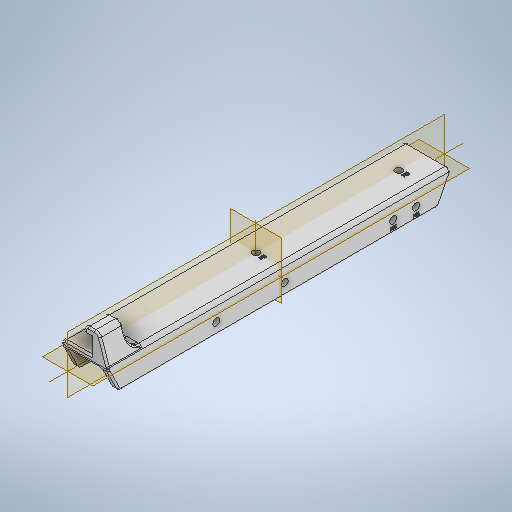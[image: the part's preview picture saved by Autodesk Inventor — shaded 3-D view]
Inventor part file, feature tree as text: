
AUTODESK INVENTOR PART (.ipt)
format: ipt  version: 2025 (Build 290162000, 162)  size: 669,696 bytes
history: native  units: mm
features: sketch x7, fillet x6, hole x3, pattern_linear x3, extrude x2, chamfer x2, emboss x2, projected_geometry x1
ambient origin geometry x8: Origin, YZ Plane, XZ Plane, XY Plane, X Axis, Y Axis, Z Axis, Center Point
bodies: Solid1 (feature_tree)
feature tree (26):
  extrude  "Extrusion1"  Depth=30.2mm
  chamfer  "Chamfer1"  Distance=300.0mm
  chamfer  "Chamfer2"  Distance=10.0mm Angle=60.0deg
  fillet  "Fillet1"  Radius=5.0mm
  hole  "Hole1"  [1 undecoded]
  hole  "Hole2"  [1 undecoded]
  emboss  "Emboss1"
  emboss  "Emboss2"
  fillet  "Fillet4"  Radius=1.5mm
  pattern_linear  "Rectangular Pattern1"  Spacing1=4.0mm  [1 undecoded]
  pattern_linear  "Rectangular Pattern2"  Spacing1=25.0mm  [1 undecoded]
  extrude  "Extrusion4"  Depth=10.0mm
  fillet  "Fillet5"  Radius=29.95mm
  fillet  "Fillet6"  Radius=20.0mm
  fillet  "Fillet7"  Radius=15.2mm
  fillet  "Fillet8"  Radius=7.1mm
  hole  "Hole3"  [1 undecoded]
  pattern_linear  "Rectangular Pattern3"  Spacing1=12.0mm  [1 undecoded]
  sketch  "Sketch1"  dims[d0=20.0mm d1=30.2mm]
  sketch  "Sketch2"  dims[d2=5.0mm]
  sketch  "Sketch3"  dims[d3=2.0mm]
  sketch  "Sketch4"  dims[d4=3.0mm d5=300.0mm d6=0.0mm d7=20.0mm d8=10.0mm d9=60.0deg]
  sketch  "Sketch5"  dims[d10=20.0mm d11=10.0mm d12=60.0deg d13=5.0mm]
  sketch  "Sketch8"  dims[d14=6.0mm d15=6.0mm d16=4.0mm d17=2.0mm d18=90.0deg d19=8.0mm d20=20.594885mm d21=10.0mm]
  projected_geometry  "Projected Loop1"
  sketch  "Sketch9"  dims[d23=6.0mm d24=6.0mm d25=4.0mm d26=2.0mm d27=90.0deg d28=8.0mm d29=20.594885mm d31=1.5mm d32=0.0mm d33=1.5mm d34=0.0mm d42=4.0mm d44=25.0mm d45=20.0mm d47=125.0mm d48=29.95mm d49=20.0mm d51=20.0mm d52=15.2mm d53=7.1mm d54=5.0mm d55=12.0mm d56=5.0mm d57=3.0mm d58=0.5mm d59=20.0mm d60=0.0mm d61=10.0mm d62=1.5mm d63=1.5mm d64=0.5mm d65=6.0mm d66=6.0mm d67=4.0mm d68=2.0mm d69=90.0deg d70=8.0mm d71=20.594885mm d72=10.0mm d74=95.0mm d75=20.0mm d77=60.0mm d41=0.0mm d43=0.0mm]
note: 6 required parameter values undecoded (feature->parameter linkage not recoverable at this tier; creation-order binding heuristic only, values carry confidence <= 0.55)
